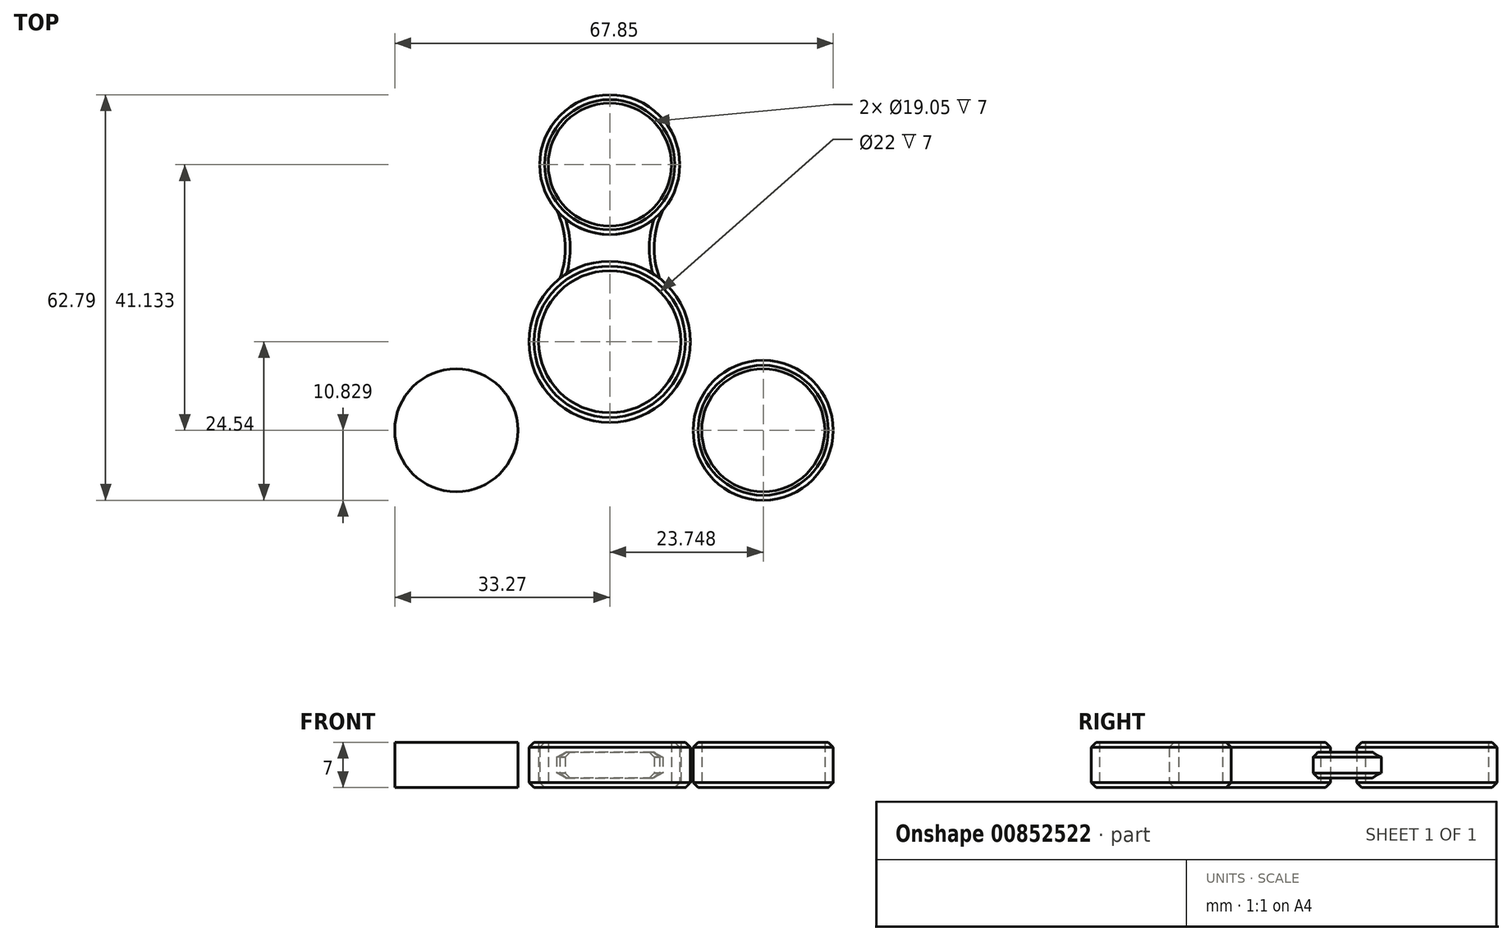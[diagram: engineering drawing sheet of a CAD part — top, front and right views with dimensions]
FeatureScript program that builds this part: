
annotation { "Feature Type Name" : "Feature", "Feature Type Description" : "" }
export const myFeature = defineFeature(function(context is Context, id is Id, definition is map)
    precondition{}
    {
        {
            var Q0;
            Q0=qCreatedBy(makeId("Top.planeOp"),FACE);
            var sketch = newSketch(context, id + "F0", { "sketchPlane" : qUnion([Q0])});
            skCircle(sketch, "E0", {"center": v(0, 27.42) * mm, "radius": 9.53 * mm});
            skCircle(sketch, "E1.MirrorC", {"center": v(-23.75, -13.71) * mm, "radius": 9.53 * mm});
            skCircle(sketch, "E2.MirrorC", {"center": v(23.75, -13.71) * mm, "radius": 9.53 * mm});
            skCircle(sketch, "E3", {"center": v(0, 0) * mm, "radius": 11 * mm});
            skCircle(sketch, "E4", {"center": v(0, 27.42) * mm, "radius": 10.83 * mm});
            skCircle(sketch, "E5.MirrorC", {"center": v(-23.75, -13.71) * mm, "radius": 10.83 * mm});
            skCircle(sketch, "E6.MirrorC", {"center": v(23.75, -13.71) * mm, "radius": 10.83 * mm});
            skCircle(sketch, "E7", {"center": v(0, 0) * mm, "radius": 12.48 * mm});
            skArc(sketch, "E8", {"start": v(8.22, 20.36) * mm, "mid": v(6.9, 15.14) * mm, "end": v(7.71, 9.8) * mm});
            skArc(sketch, "E9.MirrorCS", {"start": v(-8.22, 20.36) * mm, "mid": v(-6.9, 15.14) * mm, "end": v(-7.71, 9.8) * mm});
            skArc(sketch, "E10.MirrorCS", {"start": v(-13.53, -17.3) * mm, "mid": v(-9.66, -13.54) * mm, "end": v(-4.64, -11.58) * mm});
            skArc(sketch, "E11.MirrorCS", {"start": v(-21.75, -3.07) * mm, "mid": v(-16.56, -1.6) * mm, "end": v(-12.35, 1.77) * mm});
            skArc(sketch, "E12.MirrorCS", {"start": v(21.75, -3.07) * mm, "mid": v(16.56, -1.6) * mm, "end": v(12.35, 1.77) * mm});
            skArc(sketch, "E13.MirrorCS", {"start": v(13.53, -17.3) * mm, "mid": v(9.66, -13.54) * mm, "end": v(4.64, -11.58) * mm});
            skSolve(sketch);
        }
        {
            var Q0;
            Q0=makeQuery(id+"F0.imprint","IMPRINT",FACE,{"disambiguationData":[TD([[makeQuery(id+"F0.imprint","IMPRINT",EDGE,{"derivedFrom":sQuery(id+"F0.wireOp",EDGE,"E3")}),-1.0]])]});
            var Q1;
            Q1=makeQuery(id+"F0.imprint","IMPRINT",FACE,{"disambiguationData":[TD([[makeQuery(id+"F0.imprint","IMPRINT",EDGE,{"derivedFrom":sQuery(id+"F0.wireOp",EDGE,"E2.MirrorC")}),-1.0]])]});
            var Q2;
            Q2=makeQuery(id+"F0.imprint","IMPRINT",FACE,{"disambiguationData":[TD([[makeQuery(id+"F0.imprint","IMPRINT",EDGE,{"derivedFrom":sQuery(id+"F0.wireOp",EDGE,"E1.MirrorC")}),1.0]])]});
            var Q3;
            Q3=makeQuery(id+"F0.imprint","IMPRINT",FACE,{"disambiguationData":[TD([[makeQuery(id+"F0.imprint","IMPRINT",EDGE,{"derivedFrom":sQuery(id+"F0.wireOp",EDGE,"E0")}),-1.0]])]});
            extrude(context, id + "F1", {"entities" : qUnion([Q0, Q1, Q2, Q3]), "depth" : 7 * mm, "offsetDistance" : 25.4 * mm});
        }
        {
            var Q0;
            {var subQ0=sQuery(id+"F0.wireOp",EDGE,"E12.MirrorCS");Q0=makeQuery(id+"F0.imprint","IMPRINT",FACE,{"disambiguationData":[TD([[makeQuery(id+"F0.imprint","IMPRINT",EDGE,{"derivedFrom":subQ0}),1.0]])]});}
            var Q1;
            {var subQ0=sQuery(id+"F0.wireOp",EDGE,"E10.MirrorCS");Q1=makeQuery(id+"F0.imprint","IMPRINT",FACE,{"disambiguationData":[TD([[makeQuery(id+"F0.imprint","IMPRINT",EDGE,{"derivedFrom":subQ0}),1.0]])]});}
            var Q2;
            {var subQ0=sQuery(id+"F0.wireOp",EDGE,"E8");Q2=makeQuery(id+"F0.imprint","IMPRINT",FACE,{"disambiguationData":[TD([[makeQuery(id+"F0.imprint","IMPRINT",EDGE,{"derivedFrom":subQ0}),-1.0]])]});}
            extrude(context, id + "F2", {"entities" : qUnion([Q0, Q1, Q2]), "depth" : 4 * mm, "offsetDistance" : 25.4 * mm});
        }
        {
            var Q0;
            Q0=makeQuery(id+"F2.opExtrude","SWEPT_BODY",BODY,{"disambiguationData":[OSD([sQuery(id+"F0.wireOp",EDGE,"E4"),sQuery(id+"F0.wireOp",EDGE,"E7"),sQuery(id+"F0.wireOp",EDGE,"E8"),sQuery(id+"F0.wireOp",EDGE,"E9.MirrorCS")])]});
            var Q1;
            Q1=makeQuery(id+"F2.opExtrude","SWEPT_BODY",BODY,{"disambiguationData":[OSD([sQuery(id+"F0.wireOp",EDGE,"E5.MirrorC"),sQuery(id+"F0.wireOp",EDGE,"E7"),sQuery(id+"F0.wireOp",EDGE,"E10.MirrorCS"),sQuery(id+"F0.wireOp",EDGE,"E11.MirrorCS")])]});
            var Q2;
            Q2=makeQuery(id+"F2.opExtrude","SWEPT_BODY",BODY,{"disambiguationData":[OSD([sQuery(id+"F0.wireOp",EDGE,"E6.MirrorC"),sQuery(id+"F0.wireOp",EDGE,"E7"),sQuery(id+"F0.wireOp",EDGE,"E12.MirrorCS"),sQuery(id+"F0.wireOp",EDGE,"E13.MirrorCS")])]});
            transform(context, id + "F3", {"entities" : qUnion([Q0, Q1, Q2]), "transformType" : TransformType.TRANSLATION_3D, "dx" : 0 * mm, "dy" : 0 * mm, "dz" : 1.5 * mm, "makeCopy" : false});
        }
        {
            var Q0;
            Q0=makeQuery(id+"F1.opExtrude","CAP_EDGE",EDGE,{"disambiguationData":[OSD([sQuery(id+"F0.wireOp",EDGE,"E6.MirrorC")])],"isStart":false});
            var Q1;
            Q1=makeQuery(id+"F1.opExtrude","CAP_EDGE",EDGE,{"disambiguationData":[OSD([sQuery(id+"F0.wireOp",EDGE,"E6.MirrorC")])],"isStart":true});
            var Q2;
            Q2=makeQuery(id+"F1.opExtrude","CAP_EDGE",EDGE,{"disambiguationData":[OSD([sQuery(id+"F0.wireOp",EDGE,"E5.MirrorC")])],"isStart":true});
            var Q3;
            Q3=makeQuery(id+"F1.opExtrude","CAP_EDGE",EDGE,{"disambiguationData":[OSD([sQuery(id+"F0.wireOp",EDGE,"E5.MirrorC")])],"isStart":false});
            var Q4;
            Q4=makeQuery(id+"F1.opExtrude","CAP_EDGE",EDGE,{"disambiguationData":[OSD([sQuery(id+"F0.wireOp",EDGE,"E4")])],"isStart":false});
            var Q5;
            Q5=makeQuery(id+"F1.opExtrude","CAP_EDGE",EDGE,{"disambiguationData":[OSD([sQuery(id+"F0.wireOp",EDGE,"E4")])],"isStart":true});
            var Q6;
            Q6=makeQuery(id+"F2.opExtrude","CAP_EDGE",EDGE,{"disambiguationData":[OSD([sQuery(id+"F0.wireOp",EDGE,"E13.MirrorCS")])],"isStart":false});
            var Q7;
            Q7=makeQuery(id+"F2.opExtrude","CAP_EDGE",EDGE,{"disambiguationData":[OSD([sQuery(id+"F0.wireOp",EDGE,"E13.MirrorCS")])],"isStart":true});
            var Q8;
            Q8=makeQuery(id+"F2.opExtrude","CAP_EDGE",EDGE,{"disambiguationData":[OSD([sQuery(id+"F0.wireOp",EDGE,"E12.MirrorCS")])],"isStart":true});
            var Q9;
            Q9=makeQuery(id+"F2.opExtrude","CAP_EDGE",EDGE,{"disambiguationData":[OSD([sQuery(id+"F0.wireOp",EDGE,"E12.MirrorCS")])],"isStart":false});
            var Q10;
            Q10=makeQuery(id+"F2.opExtrude","CAP_EDGE",EDGE,{"disambiguationData":[OSD([sQuery(id+"F0.wireOp",EDGE,"E8")])],"isStart":false});
            var Q11;
            Q11=makeQuery(id+"F2.opExtrude","CAP_EDGE",EDGE,{"disambiguationData":[OSD([sQuery(id+"F0.wireOp",EDGE,"E8")])],"isStart":true});
            var Q12;
            Q12=makeQuery(id+"F2.opExtrude","CAP_EDGE",EDGE,{"disambiguationData":[OSD([sQuery(id+"F0.wireOp",EDGE,"E9.MirrorCS")])],"isStart":true});
            var Q13;
            Q13=makeQuery(id+"F2.opExtrude","CAP_EDGE",EDGE,{"disambiguationData":[OSD([sQuery(id+"F0.wireOp",EDGE,"E9.MirrorCS")])],"isStart":false});
            var Q14;
            Q14=makeQuery(id+"F2.opExtrude","CAP_EDGE",EDGE,{"disambiguationData":[OSD([sQuery(id+"F0.wireOp",EDGE,"E10.MirrorCS")])],"isStart":true});
            var Q15;
            Q15=makeQuery(id+"F2.opExtrude","CAP_EDGE",EDGE,{"disambiguationData":[OSD([sQuery(id+"F0.wireOp",EDGE,"E10.MirrorCS")])],"isStart":false});
            var Q16;
            Q16=makeQuery(id+"F2.opExtrude","CAP_EDGE",EDGE,{"disambiguationData":[OSD([sQuery(id+"F0.wireOp",EDGE,"E11.MirrorCS")])],"isStart":false});
            var Q17;
            Q17=makeQuery(id+"F2.opExtrude","CAP_EDGE",EDGE,{"disambiguationData":[OSD([sQuery(id+"F0.wireOp",EDGE,"E11.MirrorCS")])],"isStart":true});
            chamfer(context, id + "F4", {"entities" : qUnion([Q0, Q1, Q2, Q3, Q4, Q5, Q6, Q7, Q8, Q9, Q10, Q11, Q12, Q13, Q14, Q15, Q16, Q17]), "width" : 0.76 * mm, "tangentPropagation" : true});
        }
        {
            var Q0;
            Q0=makeQuery(id+"F1.opExtrude","CAP_EDGE",EDGE,{"disambiguationData":[OSD([sQuery(id+"F0.wireOp",EDGE,"E7")])],"isStart":true});
            var Q1;
            Q1=makeQuery(id+"F1.opExtrude","CAP_EDGE",EDGE,{"disambiguationData":[OSD([sQuery(id+"F0.wireOp",EDGE,"E7")])],"isStart":false});
            chamfer(context, id + "F5", {"entities" : qUnion([Q0, Q1]), "width" : 0.76 * mm, "tangentPropagation" : true});
        }
    });
